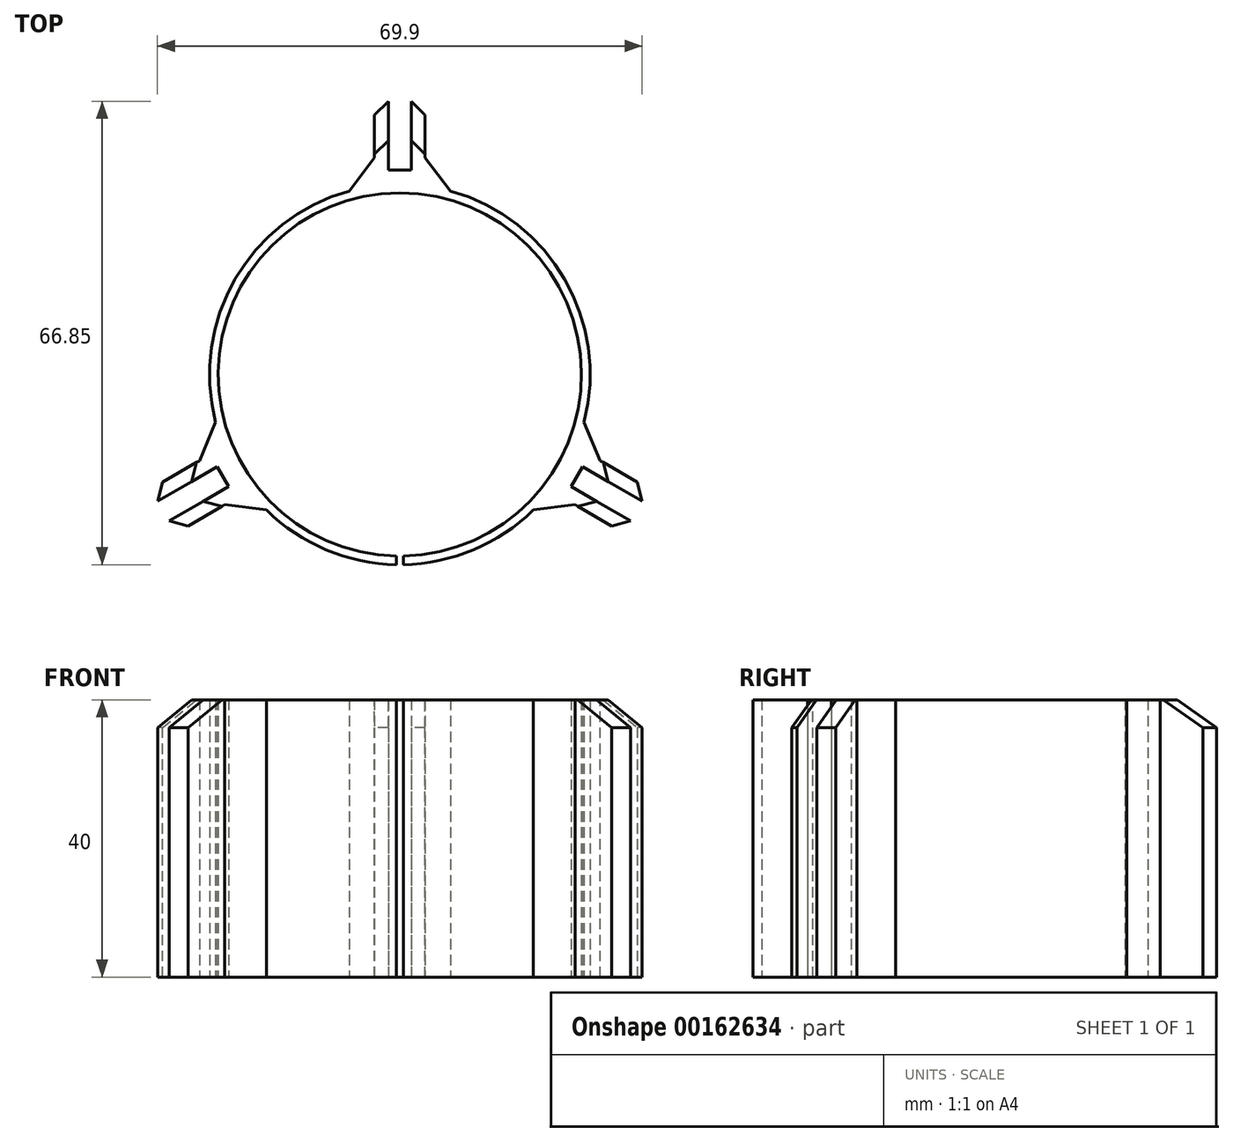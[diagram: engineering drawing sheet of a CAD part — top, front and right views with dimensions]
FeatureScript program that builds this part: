
annotation { "Feature Type Name" : "Feature", "Feature Type Description" : "" }
export const myFeature = defineFeature(function(context is Context, id is Id, definition is map)
    precondition{}
    {
        {
            var Q0;
            Q0=qCreatedBy(makeId("Top.planeOp"),FACE);
            var sketch = newSketch(context, id + "F0", { "sketchPlane" : qUnion([Q0])});
            skCircle(sketch, "E0", {"center": v(0, 0) * mm, "radius": 26.2 * mm});
            skCircle(sketch, "E1", {"center": v(0, 0) * mm, "radius": 27.45 * mm});
            skLineSegment(sketch, "E2", {"start": v(1.65, 27.4) * mm, "end": v(1.65, 39.4) * mm});
            skLineSegment(sketch, "E3", {"start": v(1.65, 39.4) * mm, "end": v(3.65, 39.4) * mm});
            skLineSegment(sketch, "E4", {"start": v(3.65, 39.4) * mm, "end": v(3.65, 27.2) * mm});
            skLineSegment(sketch, "E5.MirrorCS", {"start": v(-1.65, 27.4) * mm, "end": v(-1.65, 39.4) * mm});
            skLineSegment(sketch, "E6.MirrorCS", {"start": v(-1.65, 39.4) * mm, "end": v(-3.65, 39.4) * mm});
            skLineSegment(sketch, "E7.MirrorCS", {"start": v(-3.65, 39.4) * mm, "end": v(-3.65, 27.2) * mm});
            skLineSegment(sketch, "E8.1.0", {"start": v(-35.95, -16.54) * mm, "end": v(-25.39, -10.44) * mm});
            skLineSegment(sketch, "E8.1.1", {"start": v(-22.9, -15.13) * mm, "end": v(-33.3, -21.13) * mm});
            skLineSegment(sketch, "E8.1.2", {"start": v(-33.3, -21.13) * mm, "end": v(-32.3, -22.86) * mm});
            skLineSegment(sketch, "E8.1.3", {"start": v(-34.95, -18.27) * mm, "end": v(-35.95, -16.54) * mm});
            skLineSegment(sketch, "E8.1.4", {"start": v(-32.3, -22.86) * mm, "end": v(-21.74, -16.76) * mm});
            skLineSegment(sketch, "E8.1.5", {"start": v(-24.55, -12.27) * mm, "end": v(-34.95, -18.27) * mm});
            skLineSegment(sketch, "E8.2.0", {"start": v(32.3, -22.86) * mm, "end": v(21.74, -16.76) * mm});
            skLineSegment(sketch, "E8.2.1", {"start": v(24.55, -12.27) * mm, "end": v(34.95, -18.27) * mm});
            skLineSegment(sketch, "E8.2.2", {"start": v(34.95, -18.27) * mm, "end": v(35.95, -16.54) * mm});
            skLineSegment(sketch, "E8.2.3", {"start": v(33.3, -21.13) * mm, "end": v(32.3, -22.86) * mm});
            skLineSegment(sketch, "E8.2.4", {"start": v(35.95, -16.54) * mm, "end": v(25.39, -10.44) * mm});
            skLineSegment(sketch, "E8.2.5", {"start": v(22.9, -15.13) * mm, "end": v(33.3, -21.13) * mm});
            skLineSegment(sketch, "E9", {"start": v(-1.65, 29.5) * mm, "end": v(1.65, 29.5) * mm});
            skLineSegment(sketch, "E10.1.0", {"start": v(-24.72, -16.18) * mm, "end": v(-26.37, -13.32) * mm});
            skLineSegment(sketch, "E10.2.0", {"start": v(26.37, -13.32) * mm, "end": v(24.72, -16.18) * mm});
            skLineSegment(sketch, "E11", {"start": v(-0.5, -26.2) * mm, "end": v(-0.5, -27.45) * mm});
            skLineSegment(sketch, "E12.MirrorCS", {"start": v(0.5, -26.2) * mm, "end": v(0.5, -27.45) * mm});
            skLineSegment(sketch, "E13", {"start": v(1.65, 29.5) * mm, "end": v(3.65, 29.5) * mm});
            skLineSegment(sketch, "E14", {"start": v(-1.65, 29.5) * mm, "end": v(-3.65, 29.5) * mm});
            skLineSegment(sketch, "E15.1.0", {"start": v(-24.72, -16.18) * mm, "end": v(-23.72, -17.91) * mm});
            skLineSegment(sketch, "E15.1.1", {"start": v(-26.37, -13.32) * mm, "end": v(-27.37, -11.59) * mm});
            skLineSegment(sketch, "E15.2.0", {"start": v(26.37, -13.32) * mm, "end": v(27.37, -11.59) * mm});
            skLineSegment(sketch, "E15.2.1", {"start": v(24.72, -16.18) * mm, "end": v(23.72, -17.91) * mm});
            skSolve(sketch);
        }
        {
            var Q0;
            {var subQ0=sQuery(id+"F0.wireOp",EDGE,"E8.1.0");Q0=makeQuery(id+"F0.imprint","IMPRINT",FACE,{"disambiguationData":[TD([[makeQuery(id+"F0.imprint","IMPRINT",EDGE,{"derivedFrom":subQ0}),-1.0]])]});}
            var Q1;
            {var subQ0=sQuery(id+"F0.wireOp",EDGE,"E8.1.1");Q1=makeQuery(id+"F0.imprint","IMPRINT",FACE,{"disambiguationData":[TD([[makeQuery(id+"F0.imprint","IMPRINT",EDGE,{"derivedFrom":subQ0}),1.0]])]});}
            var Q2;
            {var subQ0=sQuery(id+"F0.wireOp",EDGE,"E8.2.0");Q2=makeQuery(id+"F0.imprint","IMPRINT",FACE,{"disambiguationData":[TD([[makeQuery(id+"F0.imprint","IMPRINT",EDGE,{"derivedFrom":subQ0}),-1.0]])]});}
            var Q3;
            {var subQ0=sQuery(id+"F0.wireOp",EDGE,"E8.2.1");Q3=makeQuery(id+"F0.imprint","IMPRINT",FACE,{"disambiguationData":[TD([[makeQuery(id+"F0.imprint","IMPRINT",EDGE,{"derivedFrom":subQ0}),1.0]])]});}
            var Q4;
            {var subQ0=sQuery(id+"F0.wireOp",EDGE,"E2");Q4=makeQuery(id+"F0.imprint","IMPRINT",FACE,{"disambiguationData":[TD([[makeQuery(id+"F0.imprint","IMPRINT",EDGE,{"derivedFrom":subQ0}),-1.0]])]});}
            var Q5;
            {var subQ0=sQuery(id+"F0.wireOp",EDGE,"E5.MirrorCS");Q5=makeQuery(id+"F0.imprint","IMPRINT",FACE,{"disambiguationData":[TD([[makeQuery(id+"F0.imprint","IMPRINT",EDGE,{"derivedFrom":subQ0}),1.0]])]});}
            var Q6;
            {var subQ5=sQuery(id+"F0.wireOp",EDGE,"E10.1.0");Q6=makeQuery(id+"F0.imprint","IMPRINT",FACE,{"disambiguationData":[TD([[makeQuery(id+"F0.imprint","IMPRINT",EDGE,{"derivedFrom":subQ5}),-1.0]])]});}
            var Q7;
            {var subQ5=sQuery(id+"F0.wireOp",EDGE,"E9");Q7=makeQuery(id+"F0.imprint","IMPRINT",FACE,{"disambiguationData":[TD([[makeQuery(id+"F0.imprint","IMPRINT",EDGE,{"derivedFrom":subQ5}),-1.0]])]});}
            var Q8;
            {var subQ5=sQuery(id+"F0.wireOp",EDGE,"E10.2.0");Q8=makeQuery(id+"F0.imprint","IMPRINT",FACE,{"disambiguationData":[TD([[makeQuery(id+"F0.imprint","IMPRINT",EDGE,{"derivedFrom":subQ5}),-1.0]])]});}
            var Q9;
            {var subQ10=sQuery(id+"F0.wireOp",EDGE,"E11");Q9=makeQuery(id+"F0.imprint","IMPRINT",FACE,{"disambiguationData":[TD([[makeQuery(id+"F0.imprint","IMPRINT",EDGE,{"derivedFrom":subQ10}),-1.0]])]});}
            extrude(context, id + "F1", {"entities" : qUnion([Q0, Q1, Q2, Q3, Q4, Q5, Q6, Q7, Q8, Q9]), "depth" : 40 * mm});
        }
        {
            var Q0;
            Q0=makeQuery(id+"F1.opExtrude","SWEPT_EDGE",EDGE,{"disambiguationData":[OSD([sQuery(id+"F0.wireOp",EDGE,"E8.1.2"),sQuery(id+"F0.wireOp",EDGE,"E8.1.4")])]});
            var Q1;
            Q1=makeQuery(id+"F1.opExtrude","SWEPT_EDGE",EDGE,{"disambiguationData":[OSD([sQuery(id+"F0.wireOp",EDGE,"E8.1.0"),sQuery(id+"F0.wireOp",EDGE,"E8.1.3")])]});
            var Q2;
            Q2=makeQuery(id+"F1.opExtrude","SWEPT_EDGE",EDGE,{"disambiguationData":[OSD([sQuery(id+"F0.wireOp",EDGE,"E8.2.0"),sQuery(id+"F0.wireOp",EDGE,"E8.2.3")])]});
            var Q3;
            Q3=makeQuery(id+"F1.opExtrude","SWEPT_EDGE",EDGE,{"disambiguationData":[OSD([sQuery(id+"F0.wireOp",EDGE,"E8.2.2"),sQuery(id+"F0.wireOp",EDGE,"E8.2.4")])]});
            var Q4;
            Q4=makeQuery(id+"F1.opExtrude","SWEPT_EDGE",EDGE,{"disambiguationData":[OSD([sQuery(id+"F0.wireOp",EDGE,"E6.MirrorCS"),sQuery(id+"F0.wireOp",EDGE,"E7.MirrorCS")])]});
            var Q5;
            Q5=makeQuery(id+"F1.opExtrude","SWEPT_EDGE",EDGE,{"disambiguationData":[OSD([sQuery(id+"F0.wireOp",EDGE,"E3"),sQuery(id+"F0.wireOp",EDGE,"E4")])]});
            chamfer(context, id + "F2", {"entities" : qUnion([Q0, Q1, Q2, Q3, Q4, Q5]), "width" : 2 * mm, "tangentPropagation" : true});
        }
        {
            var Q0;
            {var subQ0=sQuery(id+"F0.wireOp",EDGE,"E8.2.3");var subQ1=sQuery(id+"F0.wireOp",EDGE,"E8.2.0");Q0=makeQuery(id+"F2.opChamfer","BLEND_EDGE",EDGE,{"blendedFrom":[makeQuery(id+"F1.opExtrude","SWEPT_EDGE",EDGE,{"disambiguationData":[OSD([subQ1,subQ0])]}),makeQuery(id+"F1.opExtrude","CAP_FACE",FACE,{"disambiguationData":[OSD([sQuery(id+"F0.wireOp",EDGE,"E0"),sQuery(id+"F0.wireOp",EDGE,"E1"),sQuery(id+"F0.wireOp",EDGE,"E2"),sQuery(id+"F0.wireOp",EDGE,"E3"),sQuery(id+"F0.wireOp",EDGE,"E4"),sQuery(id+"F0.wireOp",EDGE,"E5.MirrorCS"),sQuery(id+"F0.wireOp",EDGE,"E6.MirrorCS"),sQuery(id+"F0.wireOp",EDGE,"E7.MirrorCS"),sQuery(id+"F0.wireOp",EDGE,"E8.1.0"),sQuery(id+"F0.wireOp",EDGE,"E8.1.1"),sQuery(id+"F0.wireOp",EDGE,"E8.1.2"),sQuery(id+"F0.wireOp",EDGE,"E8.1.3"),sQuery(id+"F0.wireOp",EDGE,"E8.1.4"),sQuery(id+"F0.wireOp",EDGE,"E8.1.5"),subQ1,sQuery(id+"F0.wireOp",EDGE,"E8.2.1"),sQuery(id+"F0.wireOp",EDGE,"E8.2.2"),subQ0,sQuery(id+"F0.wireOp",EDGE,"E8.2.4"),sQuery(id+"F0.wireOp",EDGE,"E8.2.5"),sQuery(id+"F0.wireOp",EDGE,"E9"),sQuery(id+"F0.wireOp",EDGE,"E10.1.0"),sQuery(id+"F0.wireOp",EDGE,"E10.2.0"),sQuery(id+"F0.wireOp",EDGE,"E11"),sQuery(id+"F0.wireOp",EDGE,"E12.MirrorCS")])],"isStart":false})],"blendedInto":[makeQuery(id+"F1.opExtrude","CAP_FACE",FACE,{"disambiguationData":[OSD([sQuery(id+"F0.wireOp",EDGE,"E0"),sQuery(id+"F0.wireOp",EDGE,"E1"),sQuery(id+"F0.wireOp",EDGE,"E2"),sQuery(id+"F0.wireOp",EDGE,"E3"),sQuery(id+"F0.wireOp",EDGE,"E4"),sQuery(id+"F0.wireOp",EDGE,"E5.MirrorCS"),sQuery(id+"F0.wireOp",EDGE,"E6.MirrorCS"),sQuery(id+"F0.wireOp",EDGE,"E7.MirrorCS"),sQuery(id+"F0.wireOp",EDGE,"E8.1.0"),sQuery(id+"F0.wireOp",EDGE,"E8.1.1"),sQuery(id+"F0.wireOp",EDGE,"E8.1.2"),sQuery(id+"F0.wireOp",EDGE,"E8.1.3"),sQuery(id+"F0.wireOp",EDGE,"E8.1.4"),sQuery(id+"F0.wireOp",EDGE,"E8.1.5"),subQ1,sQuery(id+"F0.wireOp",EDGE,"E8.2.1"),sQuery(id+"F0.wireOp",EDGE,"E8.2.2"),subQ0,sQuery(id+"F0.wireOp",EDGE,"E8.2.4"),sQuery(id+"F0.wireOp",EDGE,"E8.2.5"),sQuery(id+"F0.wireOp",EDGE,"E9"),sQuery(id+"F0.wireOp",EDGE,"E10.1.0"),sQuery(id+"F0.wireOp",EDGE,"E10.2.0"),sQuery(id+"F0.wireOp",EDGE,"E11"),sQuery(id+"F0.wireOp",EDGE,"E12.MirrorCS")])],"isStart":false})]});}
            var Q1;
            {var subQ0=sQuery(id+"F0.wireOp",EDGE,"E8.2.4");var subQ1=sQuery(id+"F0.wireOp",EDGE,"E8.2.2");Q1=makeQuery(id+"F2.opChamfer","BLEND_EDGE",EDGE,{"blendedFrom":[makeQuery(id+"F1.opExtrude","SWEPT_EDGE",EDGE,{"disambiguationData":[OSD([subQ1,subQ0])]}),makeQuery(id+"F1.opExtrude","CAP_FACE",FACE,{"disambiguationData":[OSD([sQuery(id+"F0.wireOp",EDGE,"E0"),sQuery(id+"F0.wireOp",EDGE,"E1"),sQuery(id+"F0.wireOp",EDGE,"E2"),sQuery(id+"F0.wireOp",EDGE,"E3"),sQuery(id+"F0.wireOp",EDGE,"E4"),sQuery(id+"F0.wireOp",EDGE,"E5.MirrorCS"),sQuery(id+"F0.wireOp",EDGE,"E6.MirrorCS"),sQuery(id+"F0.wireOp",EDGE,"E7.MirrorCS"),sQuery(id+"F0.wireOp",EDGE,"E8.1.0"),sQuery(id+"F0.wireOp",EDGE,"E8.1.1"),sQuery(id+"F0.wireOp",EDGE,"E8.1.2"),sQuery(id+"F0.wireOp",EDGE,"E8.1.3"),sQuery(id+"F0.wireOp",EDGE,"E8.1.4"),sQuery(id+"F0.wireOp",EDGE,"E8.1.5"),sQuery(id+"F0.wireOp",EDGE,"E8.2.0"),sQuery(id+"F0.wireOp",EDGE,"E8.2.1"),subQ1,sQuery(id+"F0.wireOp",EDGE,"E8.2.3"),subQ0,sQuery(id+"F0.wireOp",EDGE,"E8.2.5"),sQuery(id+"F0.wireOp",EDGE,"E9"),sQuery(id+"F0.wireOp",EDGE,"E10.1.0"),sQuery(id+"F0.wireOp",EDGE,"E10.2.0"),sQuery(id+"F0.wireOp",EDGE,"E11"),sQuery(id+"F0.wireOp",EDGE,"E12.MirrorCS")])],"isStart":false})],"blendedInto":[makeQuery(id+"F1.opExtrude","CAP_FACE",FACE,{"disambiguationData":[OSD([sQuery(id+"F0.wireOp",EDGE,"E0"),sQuery(id+"F0.wireOp",EDGE,"E1"),sQuery(id+"F0.wireOp",EDGE,"E2"),sQuery(id+"F0.wireOp",EDGE,"E3"),sQuery(id+"F0.wireOp",EDGE,"E4"),sQuery(id+"F0.wireOp",EDGE,"E5.MirrorCS"),sQuery(id+"F0.wireOp",EDGE,"E6.MirrorCS"),sQuery(id+"F0.wireOp",EDGE,"E7.MirrorCS"),sQuery(id+"F0.wireOp",EDGE,"E8.1.0"),sQuery(id+"F0.wireOp",EDGE,"E8.1.1"),sQuery(id+"F0.wireOp",EDGE,"E8.1.2"),sQuery(id+"F0.wireOp",EDGE,"E8.1.3"),sQuery(id+"F0.wireOp",EDGE,"E8.1.4"),sQuery(id+"F0.wireOp",EDGE,"E8.1.5"),sQuery(id+"F0.wireOp",EDGE,"E8.2.0"),sQuery(id+"F0.wireOp",EDGE,"E8.2.1"),subQ1,sQuery(id+"F0.wireOp",EDGE,"E8.2.3"),subQ0,sQuery(id+"F0.wireOp",EDGE,"E8.2.5"),sQuery(id+"F0.wireOp",EDGE,"E9"),sQuery(id+"F0.wireOp",EDGE,"E10.1.0"),sQuery(id+"F0.wireOp",EDGE,"E10.2.0"),sQuery(id+"F0.wireOp",EDGE,"E11"),sQuery(id+"F0.wireOp",EDGE,"E12.MirrorCS")])],"isStart":false})]});}
            var Q2;
            {var subQ0=sQuery(id+"F0.wireOp",EDGE,"E8.1.4");var subQ1=sQuery(id+"F0.wireOp",EDGE,"E8.1.2");Q2=makeQuery(id+"F2.opChamfer","BLEND_EDGE",EDGE,{"blendedFrom":[makeQuery(id+"F1.opExtrude","SWEPT_EDGE",EDGE,{"disambiguationData":[OSD([subQ1,subQ0])]}),makeQuery(id+"F1.opExtrude","CAP_FACE",FACE,{"disambiguationData":[OSD([sQuery(id+"F0.wireOp",EDGE,"E0"),sQuery(id+"F0.wireOp",EDGE,"E1"),sQuery(id+"F0.wireOp",EDGE,"E2"),sQuery(id+"F0.wireOp",EDGE,"E3"),sQuery(id+"F0.wireOp",EDGE,"E4"),sQuery(id+"F0.wireOp",EDGE,"E5.MirrorCS"),sQuery(id+"F0.wireOp",EDGE,"E6.MirrorCS"),sQuery(id+"F0.wireOp",EDGE,"E7.MirrorCS"),sQuery(id+"F0.wireOp",EDGE,"E8.1.0"),sQuery(id+"F0.wireOp",EDGE,"E8.1.1"),subQ1,sQuery(id+"F0.wireOp",EDGE,"E8.1.3"),subQ0,sQuery(id+"F0.wireOp",EDGE,"E8.1.5"),sQuery(id+"F0.wireOp",EDGE,"E8.2.0"),sQuery(id+"F0.wireOp",EDGE,"E8.2.1"),sQuery(id+"F0.wireOp",EDGE,"E8.2.2"),sQuery(id+"F0.wireOp",EDGE,"E8.2.3"),sQuery(id+"F0.wireOp",EDGE,"E8.2.4"),sQuery(id+"F0.wireOp",EDGE,"E8.2.5"),sQuery(id+"F0.wireOp",EDGE,"E9"),sQuery(id+"F0.wireOp",EDGE,"E10.1.0"),sQuery(id+"F0.wireOp",EDGE,"E10.2.0"),sQuery(id+"F0.wireOp",EDGE,"E11"),sQuery(id+"F0.wireOp",EDGE,"E12.MirrorCS")])],"isStart":false})],"blendedInto":[makeQuery(id+"F1.opExtrude","CAP_FACE",FACE,{"disambiguationData":[OSD([sQuery(id+"F0.wireOp",EDGE,"E0"),sQuery(id+"F0.wireOp",EDGE,"E1"),sQuery(id+"F0.wireOp",EDGE,"E2"),sQuery(id+"F0.wireOp",EDGE,"E3"),sQuery(id+"F0.wireOp",EDGE,"E4"),sQuery(id+"F0.wireOp",EDGE,"E5.MirrorCS"),sQuery(id+"F0.wireOp",EDGE,"E6.MirrorCS"),sQuery(id+"F0.wireOp",EDGE,"E7.MirrorCS"),sQuery(id+"F0.wireOp",EDGE,"E8.1.0"),sQuery(id+"F0.wireOp",EDGE,"E8.1.1"),subQ1,sQuery(id+"F0.wireOp",EDGE,"E8.1.3"),subQ0,sQuery(id+"F0.wireOp",EDGE,"E8.1.5"),sQuery(id+"F0.wireOp",EDGE,"E8.2.0"),sQuery(id+"F0.wireOp",EDGE,"E8.2.1"),sQuery(id+"F0.wireOp",EDGE,"E8.2.2"),sQuery(id+"F0.wireOp",EDGE,"E8.2.3"),sQuery(id+"F0.wireOp",EDGE,"E8.2.4"),sQuery(id+"F0.wireOp",EDGE,"E8.2.5"),sQuery(id+"F0.wireOp",EDGE,"E9"),sQuery(id+"F0.wireOp",EDGE,"E10.1.0"),sQuery(id+"F0.wireOp",EDGE,"E10.2.0"),sQuery(id+"F0.wireOp",EDGE,"E11"),sQuery(id+"F0.wireOp",EDGE,"E12.MirrorCS")])],"isStart":false})]});}
            var Q3;
            {var subQ0=sQuery(id+"F0.wireOp",EDGE,"E8.1.3");var subQ1=sQuery(id+"F0.wireOp",EDGE,"E8.1.0");Q3=makeQuery(id+"F2.opChamfer","BLEND_EDGE",EDGE,{"blendedFrom":[makeQuery(id+"F1.opExtrude","SWEPT_EDGE",EDGE,{"disambiguationData":[OSD([subQ1,subQ0])]}),makeQuery(id+"F1.opExtrude","CAP_FACE",FACE,{"disambiguationData":[OSD([sQuery(id+"F0.wireOp",EDGE,"E0"),sQuery(id+"F0.wireOp",EDGE,"E1"),sQuery(id+"F0.wireOp",EDGE,"E2"),sQuery(id+"F0.wireOp",EDGE,"E3"),sQuery(id+"F0.wireOp",EDGE,"E4"),sQuery(id+"F0.wireOp",EDGE,"E5.MirrorCS"),sQuery(id+"F0.wireOp",EDGE,"E6.MirrorCS"),sQuery(id+"F0.wireOp",EDGE,"E7.MirrorCS"),subQ1,sQuery(id+"F0.wireOp",EDGE,"E8.1.1"),sQuery(id+"F0.wireOp",EDGE,"E8.1.2"),subQ0,sQuery(id+"F0.wireOp",EDGE,"E8.1.4"),sQuery(id+"F0.wireOp",EDGE,"E8.1.5"),sQuery(id+"F0.wireOp",EDGE,"E8.2.0"),sQuery(id+"F0.wireOp",EDGE,"E8.2.1"),sQuery(id+"F0.wireOp",EDGE,"E8.2.2"),sQuery(id+"F0.wireOp",EDGE,"E8.2.3"),sQuery(id+"F0.wireOp",EDGE,"E8.2.4"),sQuery(id+"F0.wireOp",EDGE,"E8.2.5"),sQuery(id+"F0.wireOp",EDGE,"E9"),sQuery(id+"F0.wireOp",EDGE,"E10.1.0"),sQuery(id+"F0.wireOp",EDGE,"E10.2.0"),sQuery(id+"F0.wireOp",EDGE,"E11"),sQuery(id+"F0.wireOp",EDGE,"E12.MirrorCS")])],"isStart":false})],"blendedInto":[makeQuery(id+"F1.opExtrude","CAP_FACE",FACE,{"disambiguationData":[OSD([sQuery(id+"F0.wireOp",EDGE,"E0"),sQuery(id+"F0.wireOp",EDGE,"E1"),sQuery(id+"F0.wireOp",EDGE,"E2"),sQuery(id+"F0.wireOp",EDGE,"E3"),sQuery(id+"F0.wireOp",EDGE,"E4"),sQuery(id+"F0.wireOp",EDGE,"E5.MirrorCS"),sQuery(id+"F0.wireOp",EDGE,"E6.MirrorCS"),sQuery(id+"F0.wireOp",EDGE,"E7.MirrorCS"),subQ1,sQuery(id+"F0.wireOp",EDGE,"E8.1.1"),sQuery(id+"F0.wireOp",EDGE,"E8.1.2"),subQ0,sQuery(id+"F0.wireOp",EDGE,"E8.1.4"),sQuery(id+"F0.wireOp",EDGE,"E8.1.5"),sQuery(id+"F0.wireOp",EDGE,"E8.2.0"),sQuery(id+"F0.wireOp",EDGE,"E8.2.1"),sQuery(id+"F0.wireOp",EDGE,"E8.2.2"),sQuery(id+"F0.wireOp",EDGE,"E8.2.3"),sQuery(id+"F0.wireOp",EDGE,"E8.2.4"),sQuery(id+"F0.wireOp",EDGE,"E8.2.5"),sQuery(id+"F0.wireOp",EDGE,"E9"),sQuery(id+"F0.wireOp",EDGE,"E10.1.0"),sQuery(id+"F0.wireOp",EDGE,"E10.2.0"),sQuery(id+"F0.wireOp",EDGE,"E11"),sQuery(id+"F0.wireOp",EDGE,"E12.MirrorCS")])],"isStart":false})]});}
            var Q4;
            {var subQ0=sQuery(id+"F0.wireOp",EDGE,"E7.MirrorCS");var subQ1=sQuery(id+"F0.wireOp",EDGE,"E6.MirrorCS");Q4=makeQuery(id+"F2.opChamfer","BLEND_EDGE",EDGE,{"blendedFrom":[makeQuery(id+"F1.opExtrude","SWEPT_EDGE",EDGE,{"disambiguationData":[OSD([subQ1,subQ0])]}),makeQuery(id+"F1.opExtrude","CAP_FACE",FACE,{"disambiguationData":[OSD([sQuery(id+"F0.wireOp",EDGE,"E0"),sQuery(id+"F0.wireOp",EDGE,"E1"),sQuery(id+"F0.wireOp",EDGE,"E2"),sQuery(id+"F0.wireOp",EDGE,"E3"),sQuery(id+"F0.wireOp",EDGE,"E4"),sQuery(id+"F0.wireOp",EDGE,"E5.MirrorCS"),subQ1,subQ0,sQuery(id+"F0.wireOp",EDGE,"E8.1.0"),sQuery(id+"F0.wireOp",EDGE,"E8.1.1"),sQuery(id+"F0.wireOp",EDGE,"E8.1.2"),sQuery(id+"F0.wireOp",EDGE,"E8.1.3"),sQuery(id+"F0.wireOp",EDGE,"E8.1.4"),sQuery(id+"F0.wireOp",EDGE,"E8.1.5"),sQuery(id+"F0.wireOp",EDGE,"E8.2.0"),sQuery(id+"F0.wireOp",EDGE,"E8.2.1"),sQuery(id+"F0.wireOp",EDGE,"E8.2.2"),sQuery(id+"F0.wireOp",EDGE,"E8.2.3"),sQuery(id+"F0.wireOp",EDGE,"E8.2.4"),sQuery(id+"F0.wireOp",EDGE,"E8.2.5"),sQuery(id+"F0.wireOp",EDGE,"E9"),sQuery(id+"F0.wireOp",EDGE,"E10.1.0"),sQuery(id+"F0.wireOp",EDGE,"E10.2.0"),sQuery(id+"F0.wireOp",EDGE,"E11"),sQuery(id+"F0.wireOp",EDGE,"E12.MirrorCS")])],"isStart":false})],"blendedInto":[makeQuery(id+"F1.opExtrude","CAP_FACE",FACE,{"disambiguationData":[OSD([sQuery(id+"F0.wireOp",EDGE,"E0"),sQuery(id+"F0.wireOp",EDGE,"E1"),sQuery(id+"F0.wireOp",EDGE,"E2"),sQuery(id+"F0.wireOp",EDGE,"E3"),sQuery(id+"F0.wireOp",EDGE,"E4"),sQuery(id+"F0.wireOp",EDGE,"E5.MirrorCS"),subQ1,subQ0,sQuery(id+"F0.wireOp",EDGE,"E8.1.0"),sQuery(id+"F0.wireOp",EDGE,"E8.1.1"),sQuery(id+"F0.wireOp",EDGE,"E8.1.2"),sQuery(id+"F0.wireOp",EDGE,"E8.1.3"),sQuery(id+"F0.wireOp",EDGE,"E8.1.4"),sQuery(id+"F0.wireOp",EDGE,"E8.1.5"),sQuery(id+"F0.wireOp",EDGE,"E8.2.0"),sQuery(id+"F0.wireOp",EDGE,"E8.2.1"),sQuery(id+"F0.wireOp",EDGE,"E8.2.2"),sQuery(id+"F0.wireOp",EDGE,"E8.2.3"),sQuery(id+"F0.wireOp",EDGE,"E8.2.4"),sQuery(id+"F0.wireOp",EDGE,"E8.2.5"),sQuery(id+"F0.wireOp",EDGE,"E9"),sQuery(id+"F0.wireOp",EDGE,"E10.1.0"),sQuery(id+"F0.wireOp",EDGE,"E10.2.0"),sQuery(id+"F0.wireOp",EDGE,"E11"),sQuery(id+"F0.wireOp",EDGE,"E12.MirrorCS")])],"isStart":false})]});}
            var Q5;
            {var subQ0=sQuery(id+"F0.wireOp",EDGE,"E4");var subQ1=sQuery(id+"F0.wireOp",EDGE,"E3");Q5=makeQuery(id+"F2.opChamfer","BLEND_EDGE",EDGE,{"blendedFrom":[makeQuery(id+"F1.opExtrude","SWEPT_EDGE",EDGE,{"disambiguationData":[OSD([subQ1,subQ0])]}),makeQuery(id+"F1.opExtrude","CAP_FACE",FACE,{"disambiguationData":[OSD([sQuery(id+"F0.wireOp",EDGE,"E0"),sQuery(id+"F0.wireOp",EDGE,"E1"),sQuery(id+"F0.wireOp",EDGE,"E2"),subQ1,subQ0,sQuery(id+"F0.wireOp",EDGE,"E5.MirrorCS"),sQuery(id+"F0.wireOp",EDGE,"E6.MirrorCS"),sQuery(id+"F0.wireOp",EDGE,"E7.MirrorCS"),sQuery(id+"F0.wireOp",EDGE,"E8.1.0"),sQuery(id+"F0.wireOp",EDGE,"E8.1.1"),sQuery(id+"F0.wireOp",EDGE,"E8.1.2"),sQuery(id+"F0.wireOp",EDGE,"E8.1.3"),sQuery(id+"F0.wireOp",EDGE,"E8.1.4"),sQuery(id+"F0.wireOp",EDGE,"E8.1.5"),sQuery(id+"F0.wireOp",EDGE,"E8.2.0"),sQuery(id+"F0.wireOp",EDGE,"E8.2.1"),sQuery(id+"F0.wireOp",EDGE,"E8.2.2"),sQuery(id+"F0.wireOp",EDGE,"E8.2.3"),sQuery(id+"F0.wireOp",EDGE,"E8.2.4"),sQuery(id+"F0.wireOp",EDGE,"E8.2.5"),sQuery(id+"F0.wireOp",EDGE,"E9"),sQuery(id+"F0.wireOp",EDGE,"E10.1.0"),sQuery(id+"F0.wireOp",EDGE,"E10.2.0"),sQuery(id+"F0.wireOp",EDGE,"E11"),sQuery(id+"F0.wireOp",EDGE,"E12.MirrorCS")])],"isStart":false})],"blendedInto":[makeQuery(id+"F1.opExtrude","CAP_FACE",FACE,{"disambiguationData":[OSD([sQuery(id+"F0.wireOp",EDGE,"E0"),sQuery(id+"F0.wireOp",EDGE,"E1"),sQuery(id+"F0.wireOp",EDGE,"E2"),subQ1,subQ0,sQuery(id+"F0.wireOp",EDGE,"E5.MirrorCS"),sQuery(id+"F0.wireOp",EDGE,"E6.MirrorCS"),sQuery(id+"F0.wireOp",EDGE,"E7.MirrorCS"),sQuery(id+"F0.wireOp",EDGE,"E8.1.0"),sQuery(id+"F0.wireOp",EDGE,"E8.1.1"),sQuery(id+"F0.wireOp",EDGE,"E8.1.2"),sQuery(id+"F0.wireOp",EDGE,"E8.1.3"),sQuery(id+"F0.wireOp",EDGE,"E8.1.4"),sQuery(id+"F0.wireOp",EDGE,"E8.1.5"),sQuery(id+"F0.wireOp",EDGE,"E8.2.0"),sQuery(id+"F0.wireOp",EDGE,"E8.2.1"),sQuery(id+"F0.wireOp",EDGE,"E8.2.2"),sQuery(id+"F0.wireOp",EDGE,"E8.2.3"),sQuery(id+"F0.wireOp",EDGE,"E8.2.4"),sQuery(id+"F0.wireOp",EDGE,"E8.2.5"),sQuery(id+"F0.wireOp",EDGE,"E9"),sQuery(id+"F0.wireOp",EDGE,"E10.1.0"),sQuery(id+"F0.wireOp",EDGE,"E10.2.0"),sQuery(id+"F0.wireOp",EDGE,"E11"),sQuery(id+"F0.wireOp",EDGE,"E12.MirrorCS")])],"isStart":false})]});}
            chamfer(context, id + "F3", {"entities" : qUnion([Q0, Q1, Q2, Q3, Q4, Q5]), "width" : 4 * mm, "tangentPropagation" : true});
        }
        {
            var Q0;
            Q0=makeQuery(id+"F1.opExtrude","SWEPT_EDGE",EDGE,{"disambiguationData":[OSD([sQuery(id+"F0.wireOp",EDGE,"E1"),sQuery(id+"F0.wireOp",EDGE,"E8.1.4")])]});
            var Q1;
            Q1=makeQuery(id+"F1.opExtrude","SWEPT_EDGE",EDGE,{"disambiguationData":[OSD([sQuery(id+"F0.wireOp",EDGE,"E1"),sQuery(id+"F0.wireOp",EDGE,"E8.2.0")])]});
            var Q2;
            Q2=makeQuery(id+"F1.opExtrude","SWEPT_EDGE",EDGE,{"disambiguationData":[OSD([sQuery(id+"F0.wireOp",EDGE,"E1"),sQuery(id+"F0.wireOp",EDGE,"E8.2.4")])]});
            var Q3;
            Q3=makeQuery(id+"F1.opExtrude","SWEPT_EDGE",EDGE,{"disambiguationData":[OSD([sQuery(id+"F0.wireOp",EDGE,"E1"),sQuery(id+"F0.wireOp",EDGE,"E4")])]});
            var Q4;
            Q4=makeQuery(id+"F1.opExtrude","SWEPT_EDGE",EDGE,{"disambiguationData":[OSD([sQuery(id+"F0.wireOp",EDGE,"E1"),sQuery(id+"F0.wireOp",EDGE,"E7.MirrorCS")])]});
            var Q5;
            Q5=makeQuery(id+"F1.opExtrude","SWEPT_EDGE",EDGE,{"disambiguationData":[OSD([sQuery(id+"F0.wireOp",EDGE,"E1"),sQuery(id+"F0.wireOp",EDGE,"E8.1.0")])]});
            chamfer(context, id + "F4", {"entities" : qUnion([Q0, Q1, Q2, Q3, Q4, Q5]), "width" : 5 * mm, "tangentPropagation" : true});
        }
    });
